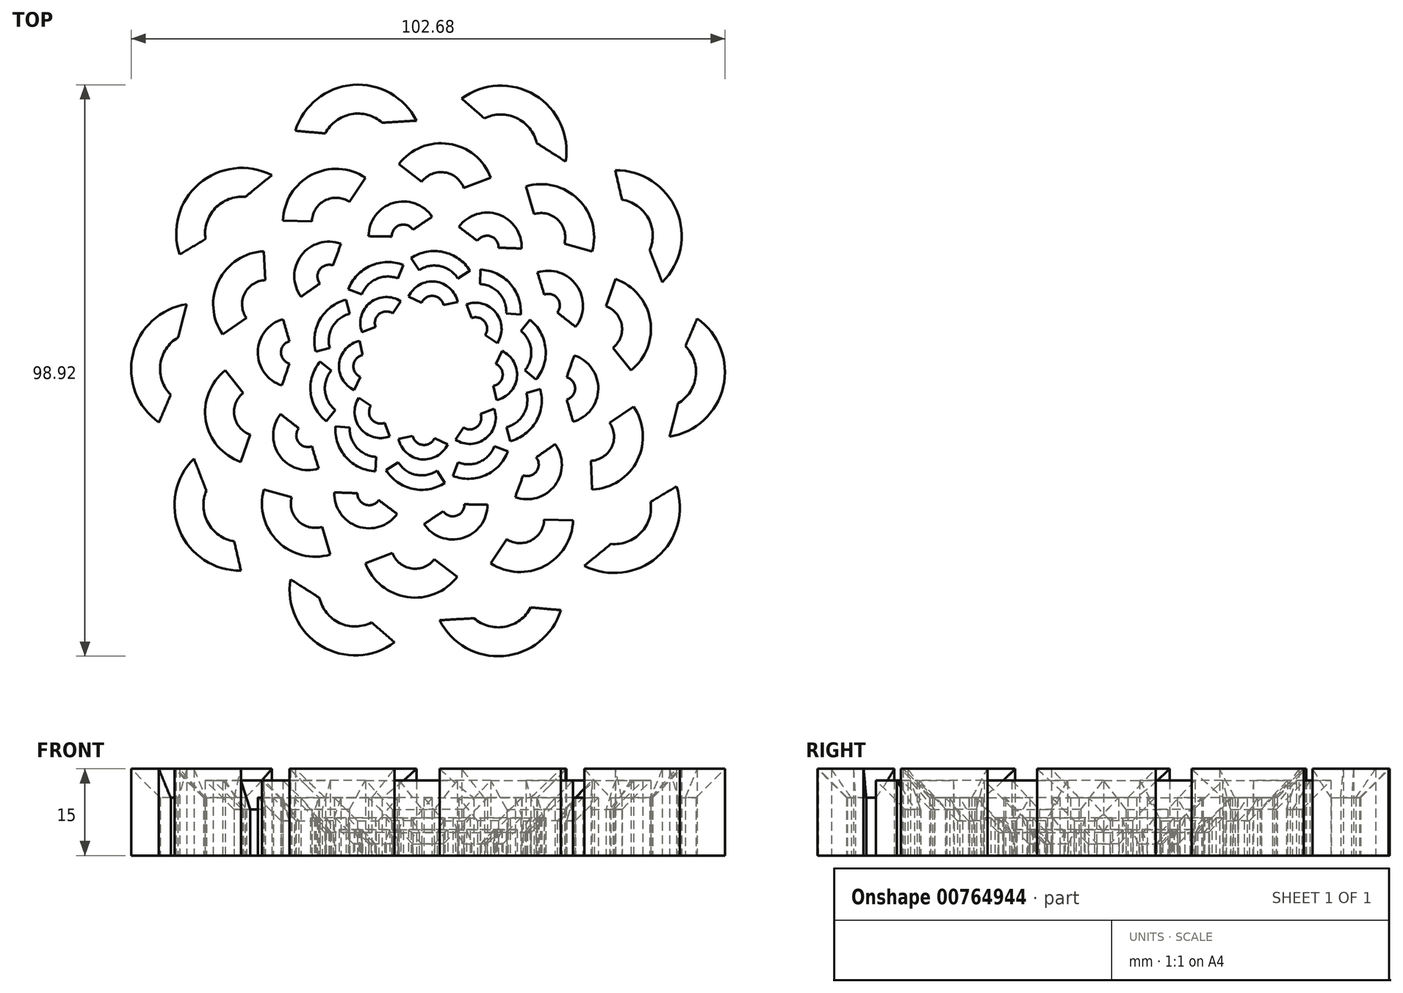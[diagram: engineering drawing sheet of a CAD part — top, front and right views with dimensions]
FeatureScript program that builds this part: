
annotation { "Feature Type Name" : "Feature", "Feature Type Description" : "" }
export const myFeature = defineFeature(function(context is Context, id is Id, definition is map)
    precondition{}
    {
        {
            var Q0;
            Q0=qCreatedBy(makeId("Top.planeOp"),FACE);
            cPlane(context, id + "F0", {"entities" : qUnion([Q0]), "cplaneType" : CPlaneType.OFFSET, "offset" : 30 * mm, "width" : 150 * mm, "height" : 150 * mm});
        }
        {
            var Q0;
            Q0=qCreatedBy(id+"F0.planeOp",FACE);
            var sketch = newSketch(context, id + "F1", { "sketchPlane" : qUnion([Q0])});
            skArc(sketch, "E0", {"start": v(-43.24, 5.7) * mm, "mid": v(-46.3, 1.06) * mm, "end": v(-44.5, -4.21) * mm});
            skArc(sketch, "E1.0", {"start": v(-41.74, 11.46) * mm, "mid": v(-51.04, 2.85) * mm, "end": v(-46.55, -9) * mm});
            skLineSegment(sketch, "E2", {"start": v(-41.74, 11.46) * mm, "end": v(-43.24, 5.7) * mm});
            skLineSegment(sketch, "E3", {"start": v(-44.5, -4.21) * mm, "end": v(-46.55, -9) * mm});
            skArc(sketch, "E4.1.0", {"start": v(-38.34, -20.8) * mm, "mid": v(-38.07, -26.36) * mm, "end": v(-33.53, -29.57) * mm});
            skLineSegment(sketch, "E4.1.1", {"start": v(-40.5, -15.26) * mm, "end": v(-38.34, -20.8) * mm});
            skLineSegment(sketch, "E4.1.2", {"start": v(-33.53, -29.57) * mm, "end": v(-32.36, -34.65) * mm});
            skArc(sketch, "E4.1.3", {"start": v(-40.5, -15.26) * mm, "mid": v(-42.97, -27.7) * mm, "end": v(-32.36, -34.65) * mm});
            skArc(sketch, "E4.2.0", {"start": v(-18.79, -39.36) * mm, "mid": v(-15.3, -43.7) * mm, "end": v(-9.75, -43.63) * mm});
            skLineSegment(sketch, "E4.2.1", {"start": v(-23.8, -36.15) * mm, "end": v(-18.79, -39.36) * mm});
            skLineSegment(sketch, "E4.2.2", {"start": v(-9.75, -43.63) * mm, "end": v(-5.82, -47.05) * mm});
            skArc(sketch, "E4.2.3", {"start": v(-23.8, -36.15) * mm, "mid": v(-18.48, -47.66) * mm, "end": v(-5.82, -47.05) * mm});
            skArc(sketch, "E4.3.0", {"start": v(7.93, -42.89) * mm, "mid": v(13.3, -44.35) * mm, "end": v(17.76, -41.02) * mm});
            skLineSegment(sketch, "E4.3.1", {"start": v(2, -43.24) * mm, "end": v(7.93, -42.89) * mm});
            skLineSegment(sketch, "E4.3.2", {"start": v(17.76, -41.02) * mm, "end": v(22.95, -41.49) * mm});
            skArc(sketch, "E4.3.3", {"start": v(2, -43.24) * mm, "mid": v(13.06, -49.42) * mm, "end": v(22.95, -41.49) * mm});
            skArc(sketch, "E4.4.0", {"start": v(31.63, -30.03) * mm, "mid": v(36.83, -28.06) * mm, "end": v(38.48, -22.75) * mm});
            skLineSegment(sketch, "E4.4.1", {"start": v(27.03, -33.8) * mm, "end": v(31.63, -30.03) * mm});
            skLineSegment(sketch, "E4.4.2", {"start": v(38.48, -22.75) * mm, "end": v(42.95, -20.07) * mm});
            skArc(sketch, "E4.4.3", {"start": v(27.03, -33.8) * mm, "mid": v(39.62, -32.3) * mm, "end": v(42.95, -20.07) * mm});
            skArc(sketch, "E4.5.0", {"start": v(43.24, -5.7) * mm, "mid": v(46.3, -1.06) * mm, "end": v(44.5, 4.21) * mm});
            skLineSegment(sketch, "E4.5.1", {"start": v(41.74, -11.46) * mm, "end": v(43.24, -5.7) * mm});
            skLineSegment(sketch, "E4.5.2", {"start": v(44.5, 4.21) * mm, "end": v(46.55, 9) * mm});
            skArc(sketch, "E4.5.3", {"start": v(41.74, -11.46) * mm, "mid": v(51.04, -2.85) * mm, "end": v(46.55, 9) * mm});
            skArc(sketch, "E4.6.0", {"start": v(38.34, 20.8) * mm, "mid": v(38.07, 26.36) * mm, "end": v(33.53, 29.57) * mm});
            skLineSegment(sketch, "E4.6.1", {"start": v(40.5, 15.26) * mm, "end": v(38.34, 20.8) * mm});
            skLineSegment(sketch, "E4.6.2", {"start": v(33.53, 29.57) * mm, "end": v(32.36, 34.65) * mm});
            skArc(sketch, "E4.6.3", {"start": v(40.5, 15.26) * mm, "mid": v(42.97, 27.7) * mm, "end": v(32.36, 34.65) * mm});
            skArc(sketch, "E4.7.0", {"start": v(18.79, 39.36) * mm, "mid": v(15.3, 43.7) * mm, "end": v(9.75, 43.63) * mm});
            skLineSegment(sketch, "E4.7.1", {"start": v(23.8, 36.15) * mm, "end": v(18.79, 39.36) * mm});
            skLineSegment(sketch, "E4.7.2", {"start": v(9.75, 43.63) * mm, "end": v(5.82, 47.05) * mm});
            skArc(sketch, "E4.7.3", {"start": v(23.8, 36.15) * mm, "mid": v(18.48, 47.66) * mm, "end": v(5.82, 47.05) * mm});
            skArc(sketch, "E4.8.0", {"start": v(-7.93, 42.89) * mm, "mid": v(-13.3, 44.35) * mm, "end": v(-17.76, 41.02) * mm});
            skLineSegment(sketch, "E4.8.1", {"start": v(-2, 43.24) * mm, "end": v(-7.93, 42.89) * mm});
            skLineSegment(sketch, "E4.8.2", {"start": v(-17.76, 41.02) * mm, "end": v(-22.95, 41.49) * mm});
            skArc(sketch, "E4.8.3", {"start": v(-2, 43.24) * mm, "mid": v(-13.06, 49.42) * mm, "end": v(-22.95, 41.49) * mm});
            skArc(sketch, "E4.9.0", {"start": v(-31.63, 30.03) * mm, "mid": v(-36.83, 28.06) * mm, "end": v(-38.48, 22.75) * mm});
            skLineSegment(sketch, "E4.9.1", {"start": v(-27.03, 33.8) * mm, "end": v(-31.63, 30.03) * mm});
            skLineSegment(sketch, "E4.9.2", {"start": v(-38.48, 22.75) * mm, "end": v(-42.95, 20.07) * mm});
            skArc(sketch, "E4.9.3", {"start": v(-27.03, 33.8) * mm, "mid": v(-39.62, 32.3) * mm, "end": v(-42.95, 20.07) * mm});
            skPoint(sketch, "E4.center", {"position": v(0, 0) * mm});
            skArc(sketch, "E5", {"start": v(-35.09, 0) * mm, "mid": v(-38.42, -8.7) * mm, "end": v(-32.4, -15.84) * mm});
            skArc(sketch, "E6.0", {"start": v(-31.97, -3.91) * mm, "mid": v(-33.49, -7.87) * mm, "end": v(-30.75, -11.12) * mm});
            skLineSegment(sketch, "E7", {"start": v(-35.09, 0) * mm, "end": v(-31.97, -3.91) * mm});
            skLineSegment(sketch, "E8", {"start": v(-30.75, -11.12) * mm, "end": v(-32.4, -15.84) * mm});
            skArc(sketch, "E9.1.0", {"start": v(-28.39, -20.62) * mm, "mid": v(-25.96, -29.63) * mm, "end": v(-16.9, -31.86) * mm});
            skArc(sketch, "E9.1.1", {"start": v(-23.57, -21.96) * mm, "mid": v(-22.46, -26.05) * mm, "end": v(-18.34, -27.07) * mm});
            skLineSegment(sketch, "E9.1.2", {"start": v(-28.39, -20.62) * mm, "end": v(-23.57, -21.96) * mm});
            skLineSegment(sketch, "E9.1.3", {"start": v(-18.34, -27.07) * mm, "end": v(-16.9, -31.86) * mm});
            skArc(sketch, "E9.2.0", {"start": v(-10.84, -33.37) * mm, "mid": v(-3.59, -39.23) * mm, "end": v(5.05, -35.71) * mm});
            skArc(sketch, "E9.2.1", {"start": v(-6.16, -31.62) * mm, "mid": v(-2.86, -34.28) * mm, "end": v(1.07, -32.68) * mm});
            skLineSegment(sketch, "E9.2.2", {"start": v(-10.84, -33.37) * mm, "end": v(-6.16, -31.62) * mm});
            skLineSegment(sketch, "E9.2.3", {"start": v(1.07, -32.68) * mm, "end": v(5.05, -35.71) * mm});
            skArc(sketch, "E9.3.0", {"start": v(10.84, -33.37) * mm, "mid": v(20.16, -33.85) * mm, "end": v(25.07, -25.92) * mm});
            skArc(sketch, "E9.3.1", {"start": v(13.6, -29.2) * mm, "mid": v(17.84, -29.41) * mm, "end": v(20.08, -25.81) * mm});
            skLineSegment(sketch, "E9.3.2", {"start": v(10.84, -33.37) * mm, "end": v(13.6, -29.2) * mm});
            skLineSegment(sketch, "E9.3.3", {"start": v(20.08, -25.81) * mm, "end": v(25.07, -25.92) * mm});
            skArc(sketch, "E9.4.0", {"start": v(28.39, -20.62) * mm, "mid": v(36.2, -15.53) * mm, "end": v(35.52, -6.23) * mm});
            skArc(sketch, "E9.4.1", {"start": v(28.16, -15.63) * mm, "mid": v(31.72, -13.31) * mm, "end": v(31.41, -9.08) * mm});
            skLineSegment(sketch, "E9.4.2", {"start": v(28.39, -20.62) * mm, "end": v(28.16, -15.63) * mm});
            skLineSegment(sketch, "E9.4.3", {"start": v(31.41, -9.08) * mm, "end": v(35.52, -6.23) * mm});
            skArc(sketch, "E9.5.0", {"start": v(35.09, 0) * mm, "mid": v(38.42, 8.7) * mm, "end": v(32.4, 15.84) * mm});
            skArc(sketch, "E9.5.1", {"start": v(31.97, 3.91) * mm, "mid": v(33.49, 7.87) * mm, "end": v(30.75, 11.12) * mm});
            skLineSegment(sketch, "E9.5.2", {"start": v(35.09, 0) * mm, "end": v(31.97, 3.91) * mm});
            skLineSegment(sketch, "E9.5.3", {"start": v(30.75, 11.12) * mm, "end": v(32.4, 15.84) * mm});
            skArc(sketch, "E9.6.0", {"start": v(28.39, 20.62) * mm, "mid": v(25.96, 29.63) * mm, "end": v(16.9, 31.86) * mm});
            skArc(sketch, "E9.6.1", {"start": v(23.57, 21.96) * mm, "mid": v(22.46, 26.05) * mm, "end": v(18.34, 27.07) * mm});
            skLineSegment(sketch, "E9.6.2", {"start": v(28.39, 20.62) * mm, "end": v(23.57, 21.96) * mm});
            skLineSegment(sketch, "E9.6.3", {"start": v(18.34, 27.07) * mm, "end": v(16.9, 31.86) * mm});
            skArc(sketch, "E9.7.0", {"start": v(10.84, 33.37) * mm, "mid": v(3.59, 39.23) * mm, "end": v(-5.05, 35.71) * mm});
            skArc(sketch, "E9.7.1", {"start": v(6.16, 31.62) * mm, "mid": v(2.86, 34.28) * mm, "end": v(-1.07, 32.68) * mm});
            skLineSegment(sketch, "E9.7.2", {"start": v(10.84, 33.37) * mm, "end": v(6.16, 31.62) * mm});
            skLineSegment(sketch, "E9.7.3", {"start": v(-1.07, 32.68) * mm, "end": v(-5.05, 35.71) * mm});
            skArc(sketch, "E9.8.0", {"start": v(-10.84, 33.37) * mm, "mid": v(-20.16, 33.85) * mm, "end": v(-25.07, 25.92) * mm});
            skArc(sketch, "E9.8.1", {"start": v(-13.6, 29.2) * mm, "mid": v(-17.84, 29.41) * mm, "end": v(-20.08, 25.81) * mm});
            skLineSegment(sketch, "E9.8.2", {"start": v(-10.84, 33.37) * mm, "end": v(-13.6, 29.2) * mm});
            skLineSegment(sketch, "E9.8.3", {"start": v(-20.08, 25.81) * mm, "end": v(-25.07, 25.92) * mm});
            skArc(sketch, "E9.9.0", {"start": v(-28.39, 20.62) * mm, "mid": v(-36.2, 15.53) * mm, "end": v(-35.52, 6.23) * mm});
            skArc(sketch, "E9.9.1", {"start": v(-28.16, 15.63) * mm, "mid": v(-31.72, 13.31) * mm, "end": v(-31.41, 9.08) * mm});
            skLineSegment(sketch, "E9.9.2", {"start": v(-28.39, 20.62) * mm, "end": v(-28.16, 15.63) * mm});
            skLineSegment(sketch, "E9.9.3", {"start": v(-31.41, 9.08) * mm, "end": v(-35.52, 6.23) * mm});
            skArc(sketch, "E10", {"start": v(-25.51, -7.56) * mm, "mid": v(-25.7, -14.7) * mm, "end": v(-18.93, -16.96) * mm});
            skArc(sketch, "E11.0", {"start": v(-22.36, -10.02) * mm, "mid": v(-22.4, -12.43) * mm, "end": v(-20.1, -13.13) * mm});
            skLineSegment(sketch, "E12", {"start": v(-22.36, -10.02) * mm, "end": v(-25.51, -7.56) * mm});
            skLineSegment(sketch, "E13", {"start": v(-20.1, -13.13) * mm, "end": v(-18.93, -16.96) * mm});
            skArc(sketch, "E14.1.0", {"start": v(-16.2, -21.1) * mm, "mid": v(-12.16, -27) * mm, "end": v(-5.34, -24.84) * mm});
            skLineSegment(sketch, "E14.1.1", {"start": v(-12.2, -21.25) * mm, "end": v(-16.2, -21.1) * mm});
            skArc(sketch, "E14.1.2", {"start": v(-12.2, -21.25) * mm, "mid": v(-10.82, -23.23) * mm, "end": v(-8.54, -22.43) * mm});
            skLineSegment(sketch, "E14.1.3", {"start": v(-8.54, -22.43) * mm, "end": v(-5.34, -24.84) * mm});
            skArc(sketch, "E14.2.0", {"start": v(-0.7, -26.6) * mm, "mid": v(6.03, -28.99) * mm, "end": v(10.28, -23.24) * mm});
            skLineSegment(sketch, "E14.2.1", {"start": v(2.62, -24.36) * mm, "end": v(-0.7, -26.6) * mm});
            skArc(sketch, "E14.2.2", {"start": v(2.62, -24.36) * mm, "mid": v(4.9, -25.15) * mm, "end": v(6.28, -23.17) * mm});
            skLineSegment(sketch, "E14.2.3", {"start": v(6.28, -23.17) * mm, "end": v(10.28, -23.24) * mm});
            skArc(sketch, "E14.3.0", {"start": v(15.07, -21.93) * mm, "mid": v(21.92, -19.9) * mm, "end": v(21.98, -12.76) * mm});
            skLineSegment(sketch, "E14.3.1", {"start": v(16.44, -18.17) * mm, "end": v(15.07, -21.93) * mm});
            skArc(sketch, "E14.3.2", {"start": v(16.44, -18.17) * mm, "mid": v(18.75, -17.47) * mm, "end": v(18.7, -15.05) * mm});
            skLineSegment(sketch, "E14.3.3", {"start": v(18.7, -15.05) * mm, "end": v(21.98, -12.76) * mm});
            skArc(sketch, "E14.4.0", {"start": v(25.08, -8.88) * mm, "mid": v(29.43, -3.22) * mm, "end": v(25.28, 2.6) * mm});
            skLineSegment(sketch, "E14.4.1", {"start": v(23.98, -5.04) * mm, "end": v(25.08, -8.88) * mm});
            skArc(sketch, "E14.4.2", {"start": v(23.98, -5.04) * mm, "mid": v(25.43, -3.11) * mm, "end": v(23.97, -1.19) * mm});
            skLineSegment(sketch, "E14.4.3", {"start": v(23.97, -1.19) * mm, "end": v(25.28, 2.6) * mm});
            skArc(sketch, "E14.5.0", {"start": v(25.51, 7.56) * mm, "mid": v(25.7, 14.7) * mm, "end": v(18.93, 16.96) * mm});
            skLineSegment(sketch, "E14.5.1", {"start": v(22.36, 10.02) * mm, "end": v(25.51, 7.56) * mm});
            skArc(sketch, "E14.5.2", {"start": v(22.36, 10.02) * mm, "mid": v(22.4, 12.43) * mm, "end": v(20.1, 13.13) * mm});
            skLineSegment(sketch, "E14.5.3", {"start": v(20.1, 13.13) * mm, "end": v(18.93, 16.96) * mm});
            skArc(sketch, "E14.6.0", {"start": v(16.2, 21.1) * mm, "mid": v(12.16, 27) * mm, "end": v(5.34, 24.84) * mm});
            skLineSegment(sketch, "E14.6.1", {"start": v(12.2, 21.25) * mm, "end": v(16.2, 21.1) * mm});
            skArc(sketch, "E14.6.2", {"start": v(12.2, 21.25) * mm, "mid": v(10.82, 23.23) * mm, "end": v(8.54, 22.43) * mm});
            skLineSegment(sketch, "E14.6.3", {"start": v(8.54, 22.43) * mm, "end": v(5.34, 24.84) * mm});
            skArc(sketch, "E14.7.0", {"start": v(0.7, 26.6) * mm, "mid": v(-6.03, 28.99) * mm, "end": v(-10.28, 23.24) * mm});
            skLineSegment(sketch, "E14.7.1", {"start": v(-2.62, 24.36) * mm, "end": v(0.7, 26.6) * mm});
            skArc(sketch, "E14.7.2", {"start": v(-2.62, 24.36) * mm, "mid": v(-4.9, 25.15) * mm, "end": v(-6.28, 23.17) * mm});
            skLineSegment(sketch, "E14.7.3", {"start": v(-6.28, 23.17) * mm, "end": v(-10.28, 23.24) * mm});
            skArc(sketch, "E14.8.0", {"start": v(-15.07, 21.93) * mm, "mid": v(-21.92, 19.9) * mm, "end": v(-21.98, 12.76) * mm});
            skLineSegment(sketch, "E14.8.1", {"start": v(-16.44, 18.17) * mm, "end": v(-15.07, 21.93) * mm});
            skArc(sketch, "E14.8.2", {"start": v(-16.44, 18.17) * mm, "mid": v(-18.75, 17.47) * mm, "end": v(-18.7, 15.05) * mm});
            skLineSegment(sketch, "E14.8.3", {"start": v(-18.7, 15.05) * mm, "end": v(-21.98, 12.76) * mm});
            skArc(sketch, "E14.9.0", {"start": v(-25.08, 8.88) * mm, "mid": v(-29.43, 3.22) * mm, "end": v(-25.28, -2.6) * mm});
            skLineSegment(sketch, "E14.9.1", {"start": v(-23.98, 5.04) * mm, "end": v(-25.08, 8.88) * mm});
            skArc(sketch, "E14.9.2", {"start": v(-23.98, 5.04) * mm, "mid": v(-25.43, 3.11) * mm, "end": v(-23.97, 1.19) * mm});
            skLineSegment(sketch, "E14.9.3", {"start": v(-23.97, 1.19) * mm, "end": v(-25.28, -2.6) * mm});
            skArc(sketch, "E15", {"start": v(-14.18, 12.24) * mm, "mid": v(-18.68, 8.84) * mm, "end": v(-19.4, 3.24) * mm});
            skArc(sketch, "E16.0", {"start": v(-13.56, 9.82) * mm, "mid": v(-16.52, 7.58) * mm, "end": v(-17, 3.9) * mm});
            skLineSegment(sketch, "E17", {"start": v(-14.18, 12.24) * mm, "end": v(-13.56, 9.82) * mm});
            skLineSegment(sketch, "E18", {"start": v(-17, 3.9) * mm, "end": v(-19.4, 3.24) * mm});
            skArc(sketch, "E19.1.0", {"start": v(-16.74, -0.03) * mm, "mid": v(-17.82, -3.58) * mm, "end": v(-16.05, -6.83) * mm});
            skArc(sketch, "E19.1.1", {"start": v(-18.67, 1.57) * mm, "mid": v(-20.3, -3.83) * mm, "end": v(-17.6, -8.79) * mm});
            skLineSegment(sketch, "E19.1.2", {"start": v(-18.67, 1.57) * mm, "end": v(-16.74, -0.03) * mm});
            skLineSegment(sketch, "E19.1.3", {"start": v(-16.05, -6.83) * mm, "end": v(-17.6, -8.79) * mm});
            skArc(sketch, "E19.2.0", {"start": v(-13.53, -9.86) * mm, "mid": v(-12.32, -13.37) * mm, "end": v(-8.97, -14.96) * mm});
            skArc(sketch, "E19.2.1", {"start": v(-16.02, -9.7) * mm, "mid": v(-14.18, -15.04) * mm, "end": v(-9.08, -17.46) * mm});
            skLineSegment(sketch, "E19.2.2", {"start": v(-16.02, -9.7) * mm, "end": v(-13.53, -9.86) * mm});
            skLineSegment(sketch, "E19.2.3", {"start": v(-8.97, -14.96) * mm, "end": v(-9.08, -17.46) * mm});
            skArc(sketch, "E19.3.0", {"start": v(-5.15, -15.93) * mm, "mid": v(-2.1, -18.05) * mm, "end": v(1.54, -17.37) * mm});
            skArc(sketch, "E19.3.1", {"start": v(-7.26, -17.27) * mm, "mid": v(-2.63, -20.5) * mm, "end": v(2.91, -19.46) * mm});
            skLineSegment(sketch, "E19.3.2", {"start": v(-7.26, -17.27) * mm, "end": v(-5.15, -15.93) * mm});
            skLineSegment(sketch, "E19.3.3", {"start": v(1.54, -17.37) * mm, "end": v(2.91, -19.46) * mm});
            skArc(sketch, "E19.4.0", {"start": v(5.2, -15.91) * mm, "mid": v(8.9, -15.84) * mm, "end": v(11.46, -13.15) * mm});
            skArc(sketch, "E19.4.1", {"start": v(4.28, -18.24) * mm, "mid": v(9.92, -18.13) * mm, "end": v(13.8, -14.03) * mm});
            skLineSegment(sketch, "E19.4.2", {"start": v(4.28, -18.24) * mm, "end": v(5.2, -15.91) * mm});
            skLineSegment(sketch, "E19.4.3", {"start": v(11.46, -13.15) * mm, "end": v(13.8, -14.03) * mm});
            skArc(sketch, "E19.5.0", {"start": v(13.56, -9.82) * mm, "mid": v(16.52, -7.58) * mm, "end": v(17, -3.9) * mm});
            skArc(sketch, "E19.5.1", {"start": v(14.18, -12.24) * mm, "mid": v(18.68, -8.84) * mm, "end": v(19.4, -3.24) * mm});
            skLineSegment(sketch, "E19.5.2", {"start": v(14.18, -12.24) * mm, "end": v(13.56, -9.82) * mm});
            skLineSegment(sketch, "E19.5.3", {"start": v(17, -3.9) * mm, "end": v(19.4, -3.24) * mm});
            skArc(sketch, "E19.6.0", {"start": v(16.74, 0.03) * mm, "mid": v(17.82, 3.58) * mm, "end": v(16.05, 6.83) * mm});
            skArc(sketch, "E19.6.1", {"start": v(18.67, -1.57) * mm, "mid": v(20.3, 3.83) * mm, "end": v(17.6, 8.79) * mm});
            skLineSegment(sketch, "E19.6.2", {"start": v(18.67, -1.57) * mm, "end": v(16.74, 0.03) * mm});
            skLineSegment(sketch, "E19.6.3", {"start": v(16.05, 6.83) * mm, "end": v(17.6, 8.79) * mm});
            skArc(sketch, "E19.7.0", {"start": v(13.53, 9.86) * mm, "mid": v(12.32, 13.37) * mm, "end": v(8.97, 14.96) * mm});
            skArc(sketch, "E19.7.1", {"start": v(16.02, 9.7) * mm, "mid": v(14.18, 15.04) * mm, "end": v(9.08, 17.46) * mm});
            skLineSegment(sketch, "E19.7.2", {"start": v(16.02, 9.7) * mm, "end": v(13.53, 9.86) * mm});
            skLineSegment(sketch, "E19.7.3", {"start": v(8.97, 14.96) * mm, "end": v(9.08, 17.46) * mm});
            skArc(sketch, "E19.8.0", {"start": v(5.15, 15.93) * mm, "mid": v(2.1, 18.05) * mm, "end": v(-1.54, 17.37) * mm});
            skArc(sketch, "E19.8.1", {"start": v(7.26, 17.27) * mm, "mid": v(2.63, 20.5) * mm, "end": v(-2.91, 19.46) * mm});
            skLineSegment(sketch, "E19.8.2", {"start": v(7.26, 17.27) * mm, "end": v(5.15, 15.93) * mm});
            skLineSegment(sketch, "E19.8.3", {"start": v(-1.54, 17.37) * mm, "end": v(-2.91, 19.46) * mm});
            skArc(sketch, "E19.9.0", {"start": v(-5.2, 15.91) * mm, "mid": v(-8.9, 15.84) * mm, "end": v(-11.46, 13.15) * mm});
            skArc(sketch, "E19.9.1", {"start": v(-4.28, 18.24) * mm, "mid": v(-9.92, 18.13) * mm, "end": v(-13.8, 14.03) * mm});
            skLineSegment(sketch, "E19.9.2", {"start": v(-4.28, 18.24) * mm, "end": v(-5.2, 15.91) * mm});
            skLineSegment(sketch, "E19.9.3", {"start": v(-11.46, 13.15) * mm, "end": v(-13.8, 14.03) * mm});
            skArc(sketch, "E20", {"start": v(-11.82, 5.12) * mm, "mid": v(-15.37, 1.22) * mm, "end": v(-12.78, -3.38) * mm});
            skArc(sketch, "E21.0", {"start": v(-11.31, 2.67) * mm, "mid": v(-12.9, 0.94) * mm, "end": v(-11.74, -1.1) * mm});
            skLineSegment(sketch, "E22", {"start": v(-11.82, 5.12) * mm, "end": v(-11.31, 2.67) * mm});
            skLineSegment(sketch, "E23", {"start": v(-11.74, -1.1) * mm, "end": v(-12.78, -3.38) * mm});
            skArc(sketch, "E24.1.0", {"start": v(-11.98, -4.74) * mm, "mid": v(-11.73, -10.01) * mm, "end": v(-6.65, -11.43) * mm});
            skArc(sketch, "E24.2.0", {"start": v(-5.12, -11.82) * mm, "mid": v(-1.22, -15.37) * mm, "end": v(3.38, -12.78) * mm});
            skArc(sketch, "E25.3.3.0", {"start": v(4.74, -11.98) * mm, "mid": v(10.01, -11.73) * mm, "end": v(11.43, -6.65) * mm});
            skArc(sketch, "E25.3.4.0", {"start": v(11.82, -5.12) * mm, "mid": v(15.37, -1.22) * mm, "end": v(12.78, 3.38) * mm});
            skArc(sketch, "E25.3.5.0", {"start": v(11.98, 4.74) * mm, "mid": v(11.73, 10.01) * mm, "end": v(6.65, 11.43) * mm});
            skArc(sketch, "E25.3.6.0", {"start": v(5.12, 11.82) * mm, "mid": v(1.22, 15.37) * mm, "end": v(-3.38, 12.78) * mm});
            skArc(sketch, "E25.3.7.0", {"start": v(-4.74, 11.98) * mm, "mid": v(-10.01, 11.73) * mm, "end": v(-11.43, 6.65) * mm});
            skLineSegment(sketch, "E26.1.0", {"start": v(-7.52, -9.08) * mm, "end": v(-6.65, -11.43) * mm});
            skArc(sketch, "E26.1.1", {"start": v(-9.89, -6.11) * mm, "mid": v(-9.78, -8.45) * mm, "end": v(-7.52, -9.08) * mm});
            skLineSegment(sketch, "E26.1.2", {"start": v(-11.98, -4.74) * mm, "end": v(-9.89, -6.11) * mm});
            skLineSegment(sketch, "E26.2.0", {"start": v(1.1, -11.74) * mm, "end": v(3.38, -12.78) * mm});
            skArc(sketch, "E26.2.1", {"start": v(-2.67, -11.31) * mm, "mid": v(-0.94, -12.9) * mm, "end": v(1.1, -11.74) * mm});
            skLineSegment(sketch, "E26.2.2", {"start": v(-5.12, -11.82) * mm, "end": v(-2.67, -11.31) * mm});
            skLineSegment(sketch, "E26.3.0", {"start": v(9.08, -7.52) * mm, "end": v(11.43, -6.65) * mm});
            skArc(sketch, "E26.3.1", {"start": v(6.11, -9.89) * mm, "mid": v(8.45, -9.78) * mm, "end": v(9.08, -7.52) * mm});
            skLineSegment(sketch, "E26.3.2", {"start": v(4.74, -11.98) * mm, "end": v(6.11, -9.89) * mm});
            skLineSegment(sketch, "E26.4.0", {"start": v(11.74, 1.1) * mm, "end": v(12.78, 3.38) * mm});
            skArc(sketch, "E26.4.1", {"start": v(11.31, -2.67) * mm, "mid": v(12.9, -0.94) * mm, "end": v(11.74, 1.1) * mm});
            skLineSegment(sketch, "E26.4.2", {"start": v(11.82, -5.12) * mm, "end": v(11.31, -2.67) * mm});
            skLineSegment(sketch, "E26.5.0", {"start": v(7.52, 9.08) * mm, "end": v(6.65, 11.43) * mm});
            skArc(sketch, "E26.5.1", {"start": v(9.89, 6.11) * mm, "mid": v(9.78, 8.45) * mm, "end": v(7.52, 9.08) * mm});
            skLineSegment(sketch, "E26.5.2", {"start": v(11.98, 4.74) * mm, "end": v(9.89, 6.11) * mm});
            skLineSegment(sketch, "E26.6.0", {"start": v(-1.1, 11.74) * mm, "end": v(-3.38, 12.78) * mm});
            skArc(sketch, "E26.6.1", {"start": v(2.67, 11.31) * mm, "mid": v(0.94, 12.9) * mm, "end": v(-1.1, 11.74) * mm});
            skLineSegment(sketch, "E26.6.2", {"start": v(5.12, 11.82) * mm, "end": v(2.67, 11.31) * mm});
            skLineSegment(sketch, "E26.7.0", {"start": v(-9.08, 7.52) * mm, "end": v(-11.43, 6.65) * mm});
            skArc(sketch, "E26.7.1", {"start": v(-6.11, 9.89) * mm, "mid": v(-8.45, 9.78) * mm, "end": v(-9.08, 7.52) * mm});
            skLineSegment(sketch, "E26.7.2", {"start": v(-4.74, 11.98) * mm, "end": v(-6.11, 9.89) * mm});
            skSolve(sketch);
        }
        {
            var Q0;
            Q0=makeQuery(id+"F1.imprint","IMPRINT",FACE,{"disambiguationData":[TD([[makeQuery(id+"F1.imprint","IMPRINT",EDGE,{"derivedFrom":sQuery(id+"F1.wireOp",EDGE,"E4.3.0")}),-1.0]])]});
            var Q1;
            Q1=makeQuery(id+"F1.imprint","IMPRINT",FACE,{"disambiguationData":[TD([[makeQuery(id+"F1.imprint","IMPRINT",EDGE,{"derivedFrom":sQuery(id+"F1.wireOp",EDGE,"E4.2.0")}),-1.0]])]});
            var Q2;
            Q2=makeQuery(id+"F1.imprint","IMPRINT",FACE,{"disambiguationData":[TD([[makeQuery(id+"F1.imprint","IMPRINT",EDGE,{"derivedFrom":sQuery(id+"F1.wireOp",EDGE,"E4.1.0")}),-1.0]])]});
            var Q3;
            Q3=makeQuery(id+"F1.imprint","IMPRINT",FACE,{"disambiguationData":[TD([[makeQuery(id+"F1.imprint","IMPRINT",EDGE,{"derivedFrom":sQuery(id+"F1.wireOp",EDGE,"E0")}),-1.0]])]});
            var Q4;
            Q4=makeQuery(id+"F1.imprint","IMPRINT",FACE,{"disambiguationData":[TD([[makeQuery(id+"F1.imprint","IMPRINT",EDGE,{"derivedFrom":sQuery(id+"F1.wireOp",EDGE,"E4.9.0")}),-1.0]])]});
            var Q5;
            Q5=makeQuery(id+"F1.imprint","IMPRINT",FACE,{"disambiguationData":[TD([[makeQuery(id+"F1.imprint","IMPRINT",EDGE,{"derivedFrom":sQuery(id+"F1.wireOp",EDGE,"E4.8.0")}),-1.0]])]});
            var Q6;
            Q6=makeQuery(id+"F1.imprint","IMPRINT",FACE,{"disambiguationData":[TD([[makeQuery(id+"F1.imprint","IMPRINT",EDGE,{"derivedFrom":sQuery(id+"F1.wireOp",EDGE,"E4.7.0")}),-1.0]])]});
            var Q7;
            Q7=makeQuery(id+"F1.imprint","IMPRINT",FACE,{"disambiguationData":[TD([[makeQuery(id+"F1.imprint","IMPRINT",EDGE,{"derivedFrom":sQuery(id+"F1.wireOp",EDGE,"E4.6.0")}),-1.0]])]});
            var Q8;
            Q8=makeQuery(id+"F1.imprint","IMPRINT",FACE,{"disambiguationData":[TD([[makeQuery(id+"F1.imprint","IMPRINT",EDGE,{"derivedFrom":sQuery(id+"F1.wireOp",EDGE,"E4.5.0")}),-1.0]])]});
            var Q9;
            Q9=makeQuery(id+"F1.imprint","IMPRINT",FACE,{"disambiguationData":[TD([[makeQuery(id+"F1.imprint","IMPRINT",EDGE,{"derivedFrom":sQuery(id+"F1.wireOp",EDGE,"E4.4.0")}),-1.0]])]});
            extrude(context, id + "F2", {"entities" : qUnion([Q0, Q1, Q2, Q3, Q4, Q5, Q6, Q7, Q8, Q9]), "depth" : 15 * mm, "offsetDistance" : 25 * mm});
        }
        {
            var Q0;
            Q0=makeQuery(id+"F1.imprint","IMPRINT",FACE,{"disambiguationData":[TD([[makeQuery(id+"F1.imprint","IMPRINT",EDGE,{"derivedFrom":sQuery(id+"F1.wireOp",EDGE,"E9.2.0")}),1.0]])]});
            var Q1;
            Q1=makeQuery(id+"F1.imprint","IMPRINT",FACE,{"disambiguationData":[TD([[makeQuery(id+"F1.imprint","IMPRINT",EDGE,{"derivedFrom":sQuery(id+"F1.wireOp",EDGE,"E9.1.0")}),1.0]])]});
            var Q2;
            Q2=makeQuery(id+"F1.imprint","IMPRINT",FACE,{"disambiguationData":[TD([[makeQuery(id+"F1.imprint","IMPRINT",EDGE,{"derivedFrom":sQuery(id+"F1.wireOp",EDGE,"E5")}),1.0]])]});
            var Q3;
            Q3=makeQuery(id+"F1.imprint","IMPRINT",FACE,{"disambiguationData":[TD([[makeQuery(id+"F1.imprint","IMPRINT",EDGE,{"derivedFrom":sQuery(id+"F1.wireOp",EDGE,"E9.9.0")}),1.0]])]});
            var Q4;
            Q4=makeQuery(id+"F1.imprint","IMPRINT",FACE,{"disambiguationData":[TD([[makeQuery(id+"F1.imprint","IMPRINT",EDGE,{"derivedFrom":sQuery(id+"F1.wireOp",EDGE,"E9.8.0")}),1.0]])]});
            var Q5;
            Q5=makeQuery(id+"F1.imprint","IMPRINT",FACE,{"disambiguationData":[TD([[makeQuery(id+"F1.imprint","IMPRINT",EDGE,{"derivedFrom":sQuery(id+"F1.wireOp",EDGE,"E9.7.0")}),1.0]])]});
            var Q6;
            Q6=makeQuery(id+"F1.imprint","IMPRINT",FACE,{"disambiguationData":[TD([[makeQuery(id+"F1.imprint","IMPRINT",EDGE,{"derivedFrom":sQuery(id+"F1.wireOp",EDGE,"E9.6.0")}),1.0]])]});
            var Q7;
            Q7=makeQuery(id+"F1.imprint","IMPRINT",FACE,{"disambiguationData":[TD([[makeQuery(id+"F1.imprint","IMPRINT",EDGE,{"derivedFrom":sQuery(id+"F1.wireOp",EDGE,"E9.5.0")}),1.0]])]});
            var Q8;
            Q8=makeQuery(id+"F1.imprint","IMPRINT",FACE,{"disambiguationData":[TD([[makeQuery(id+"F1.imprint","IMPRINT",EDGE,{"derivedFrom":sQuery(id+"F1.wireOp",EDGE,"E9.4.0")}),1.0]])]});
            var Q9;
            Q9=makeQuery(id+"F1.imprint","IMPRINT",FACE,{"disambiguationData":[TD([[makeQuery(id+"F1.imprint","IMPRINT",EDGE,{"derivedFrom":sQuery(id+"F1.wireOp",EDGE,"E9.3.0")}),1.0]])]});
            extrude(context, id + "F3", {"entities" : qUnion([Q0, Q1, Q2, Q3, Q4, Q5, Q6, Q7, Q8, Q9]), "depth" : 13 * mm, "offsetDistance" : 25 * mm});
        }
        {
            var Q0;
            Q0=makeQuery(id+"F1.imprint","IMPRINT",FACE,{"disambiguationData":[TD([[makeQuery(id+"F1.imprint","IMPRINT",EDGE,{"derivedFrom":sQuery(id+"F1.wireOp",EDGE,"E14.3.0")}),1.0]])]});
            var Q1;
            Q1=makeQuery(id+"F1.imprint","IMPRINT",FACE,{"disambiguationData":[TD([[makeQuery(id+"F1.imprint","IMPRINT",EDGE,{"derivedFrom":sQuery(id+"F1.wireOp",EDGE,"E14.2.0")}),1.0]])]});
            var Q2;
            Q2=makeQuery(id+"F1.imprint","IMPRINT",FACE,{"disambiguationData":[TD([[makeQuery(id+"F1.imprint","IMPRINT",EDGE,{"derivedFrom":sQuery(id+"F1.wireOp",EDGE,"E14.1.0")}),1.0]])]});
            var Q3;
            Q3=makeQuery(id+"F1.imprint","IMPRINT",FACE,{"disambiguationData":[TD([[makeQuery(id+"F1.imprint","IMPRINT",EDGE,{"derivedFrom":sQuery(id+"F1.wireOp",EDGE,"E10")}),1.0]])]});
            var Q4;
            Q4=makeQuery(id+"F1.imprint","IMPRINT",FACE,{"disambiguationData":[TD([[makeQuery(id+"F1.imprint","IMPRINT",EDGE,{"derivedFrom":sQuery(id+"F1.wireOp",EDGE,"E14.9.0")}),1.0]])]});
            var Q5;
            Q5=makeQuery(id+"F1.imprint","IMPRINT",FACE,{"disambiguationData":[TD([[makeQuery(id+"F1.imprint","IMPRINT",EDGE,{"derivedFrom":sQuery(id+"F1.wireOp",EDGE,"E14.8.0")}),1.0]])]});
            var Q6;
            Q6=makeQuery(id+"F1.imprint","IMPRINT",FACE,{"disambiguationData":[TD([[makeQuery(id+"F1.imprint","IMPRINT",EDGE,{"derivedFrom":sQuery(id+"F1.wireOp",EDGE,"E14.7.0")}),1.0]])]});
            var Q7;
            Q7=makeQuery(id+"F1.imprint","IMPRINT",FACE,{"disambiguationData":[TD([[makeQuery(id+"F1.imprint","IMPRINT",EDGE,{"derivedFrom":sQuery(id+"F1.wireOp",EDGE,"E14.6.0")}),1.0]])]});
            var Q8;
            Q8=makeQuery(id+"F1.imprint","IMPRINT",FACE,{"disambiguationData":[TD([[makeQuery(id+"F1.imprint","IMPRINT",EDGE,{"derivedFrom":sQuery(id+"F1.wireOp",EDGE,"E14.5.0")}),1.0]])]});
            var Q9;
            Q9=makeQuery(id+"F1.imprint","IMPRINT",FACE,{"disambiguationData":[TD([[makeQuery(id+"F1.imprint","IMPRINT",EDGE,{"derivedFrom":sQuery(id+"F1.wireOp",EDGE,"E14.4.0")}),1.0]])]});
            extrude(context, id + "F4", {"entities" : qUnion([Q0, Q1, Q2, Q3, Q4, Q5, Q6, Q7, Q8, Q9]), "depth" : 11 * mm, "offsetDistance" : 25 * mm});
        }
        {
            var Q0;
            Q0=makeQuery(id+"F1.imprint","IMPRINT",FACE,{"disambiguationData":[TD([[makeQuery(id+"F1.imprint","IMPRINT",EDGE,{"derivedFrom":sQuery(id+"F1.wireOp",EDGE,"E19.4.0")}),-1.0]])]});
            var Q1;
            Q1=makeQuery(id+"F1.imprint","IMPRINT",FACE,{"disambiguationData":[TD([[makeQuery(id+"F1.imprint","IMPRINT",EDGE,{"derivedFrom":sQuery(id+"F1.wireOp",EDGE,"E19.3.0")}),-1.0]])]});
            var Q2;
            Q2=makeQuery(id+"F1.imprint","IMPRINT",FACE,{"disambiguationData":[TD([[makeQuery(id+"F1.imprint","IMPRINT",EDGE,{"derivedFrom":sQuery(id+"F1.wireOp",EDGE,"E19.2.0")}),-1.0]])]});
            var Q3;
            Q3=makeQuery(id+"F1.imprint","IMPRINT",FACE,{"disambiguationData":[TD([[makeQuery(id+"F1.imprint","IMPRINT",EDGE,{"derivedFrom":sQuery(id+"F1.wireOp",EDGE,"E19.1.0")}),-1.0]])]});
            var Q4;
            Q4=makeQuery(id+"F1.imprint","IMPRINT",FACE,{"disambiguationData":[TD([[makeQuery(id+"F1.imprint","IMPRINT",EDGE,{"derivedFrom":sQuery(id+"F1.wireOp",EDGE,"E15")}),1.0]])]});
            var Q5;
            Q5=makeQuery(id+"F1.imprint","IMPRINT",FACE,{"disambiguationData":[TD([[makeQuery(id+"F1.imprint","IMPRINT",EDGE,{"derivedFrom":sQuery(id+"F1.wireOp",EDGE,"E19.9.0")}),-1.0]])]});
            var Q6;
            Q6=makeQuery(id+"F1.imprint","IMPRINT",FACE,{"disambiguationData":[TD([[makeQuery(id+"F1.imprint","IMPRINT",EDGE,{"derivedFrom":sQuery(id+"F1.wireOp",EDGE,"E19.8.0")}),-1.0]])]});
            var Q7;
            Q7=makeQuery(id+"F1.imprint","IMPRINT",FACE,{"disambiguationData":[TD([[makeQuery(id+"F1.imprint","IMPRINT",EDGE,{"derivedFrom":sQuery(id+"F1.wireOp",EDGE,"E19.7.0")}),-1.0]])]});
            var Q8;
            Q8=makeQuery(id+"F1.imprint","IMPRINT",FACE,{"disambiguationData":[TD([[makeQuery(id+"F1.imprint","IMPRINT",EDGE,{"derivedFrom":sQuery(id+"F1.wireOp",EDGE,"E19.6.0")}),-1.0]])]});
            var Q9;
            Q9=makeQuery(id+"F1.imprint","IMPRINT",FACE,{"disambiguationData":[TD([[makeQuery(id+"F1.imprint","IMPRINT",EDGE,{"derivedFrom":sQuery(id+"F1.wireOp",EDGE,"E19.5.0")}),-1.0]])]});
            extrude(context, id + "F5", {"entities" : qUnion([Q0, Q1, Q2, Q3, Q4, Q5, Q6, Q7, Q8, Q9]), "depth" : 9 * mm, "offsetDistance" : 25 * mm});
        }
        {
            var Q0;
            Q0=makeQuery(id+"F1.imprint","IMPRINT",FACE,{"disambiguationData":[TD([[makeQuery(id+"F1.imprint","IMPRINT",EDGE,{"derivedFrom":sQuery(id+"F1.wireOp",EDGE,"E25.3.3.0")}),1.0]])]});
            var Q1;
            Q1=makeQuery(id+"F1.imprint","IMPRINT",FACE,{"disambiguationData":[TD([[makeQuery(id+"F1.imprint","IMPRINT",EDGE,{"derivedFrom":sQuery(id+"F1.wireOp",EDGE,"E24.2.0")}),1.0]])]});
            var Q2;
            Q2=makeQuery(id+"F1.imprint","IMPRINT",FACE,{"disambiguationData":[TD([[makeQuery(id+"F1.imprint","IMPRINT",EDGE,{"derivedFrom":sQuery(id+"F1.wireOp",EDGE,"E24.1.0")}),1.0]])]});
            var Q3;
            Q3=makeQuery(id+"F1.imprint","IMPRINT",FACE,{"disambiguationData":[TD([[makeQuery(id+"F1.imprint","IMPRINT",EDGE,{"derivedFrom":sQuery(id+"F1.wireOp",EDGE,"E20")}),1.0]])]});
            var Q4;
            Q4=makeQuery(id+"F1.imprint","IMPRINT",FACE,{"disambiguationData":[TD([[makeQuery(id+"F1.imprint","IMPRINT",EDGE,{"derivedFrom":sQuery(id+"F1.wireOp",EDGE,"E25.3.7.0")}),1.0]])]});
            var Q5;
            Q5=makeQuery(id+"F1.imprint","IMPRINT",FACE,{"disambiguationData":[TD([[makeQuery(id+"F1.imprint","IMPRINT",EDGE,{"derivedFrom":sQuery(id+"F1.wireOp",EDGE,"E25.3.6.0")}),1.0]])]});
            var Q6;
            Q6=makeQuery(id+"F1.imprint","IMPRINT",FACE,{"disambiguationData":[TD([[makeQuery(id+"F1.imprint","IMPRINT",EDGE,{"derivedFrom":sQuery(id+"F1.wireOp",EDGE,"E25.3.5.0")}),1.0]])]});
            var Q7;
            Q7=makeQuery(id+"F1.imprint","IMPRINT",FACE,{"disambiguationData":[TD([[makeQuery(id+"F1.imprint","IMPRINT",EDGE,{"derivedFrom":sQuery(id+"F1.wireOp",EDGE,"E25.3.4.0")}),1.0]])]});
            extrude(context, id + "F6", {"entities" : qUnion([Q0, Q1, Q2, Q3, Q4, Q5, Q6, Q7]), "depth" : 7 * mm, "offsetDistance" : 25 * mm});
        }
        {
            var Q0;
            Q0=makeQuery(id+"F2.opExtrude","CAP_EDGE",EDGE,{"disambiguationData":[OSD([sQuery(id+"F1.wireOp",EDGE,"E0")])],"isStart":false});
            var Q1;
            Q1=makeQuery(id+"F3.opExtrude","CAP_EDGE",EDGE,{"disambiguationData":[OSD([sQuery(id+"F1.wireOp",EDGE,"E6.0")])],"isStart":false});
            var Q2;
            Q2=makeQuery(id+"F2.opExtrude","CAP_EDGE",EDGE,{"disambiguationData":[OSD([sQuery(id+"F1.wireOp",EDGE,"E4.1.0")])],"isStart":false});
            var Q3;
            Q3=makeQuery(id+"F3.opExtrude","CAP_EDGE",EDGE,{"disambiguationData":[OSD([sQuery(id+"F1.wireOp",EDGE,"E9.1.1")])],"isStart":false});
            var Q4;
            Q4=makeQuery(id+"F2.opExtrude","CAP_EDGE",EDGE,{"disambiguationData":[OSD([sQuery(id+"F1.wireOp",EDGE,"E4.2.0")])],"isStart":false});
            var Q5;
            Q5=makeQuery(id+"F2.opExtrude","CAP_EDGE",EDGE,{"disambiguationData":[OSD([sQuery(id+"F1.wireOp",EDGE,"E4.3.0")])],"isStart":false});
            var Q6;
            Q6=makeQuery(id+"F3.opExtrude","CAP_EDGE",EDGE,{"disambiguationData":[OSD([sQuery(id+"F1.wireOp",EDGE,"E9.2.1")])],"isStart":false});
            var Q7;
            Q7=makeQuery(id+"F4.opExtrude","CAP_EDGE",EDGE,{"disambiguationData":[OSD([sQuery(id+"F1.wireOp",EDGE,"E14.1.2")])],"isStart":false});
            var Q8;
            Q8=makeQuery(id+"F4.opExtrude","CAP_EDGE",EDGE,{"disambiguationData":[OSD([sQuery(id+"F1.wireOp",EDGE,"E11.0")])],"isStart":false});
            var Q9;
            Q9=makeQuery(id+"F4.opExtrude","CAP_EDGE",EDGE,{"disambiguationData":[OSD([sQuery(id+"F1.wireOp",EDGE,"E14.9.2")])],"isStart":false});
            var Q10;
            Q10=makeQuery(id+"F4.opExtrude","CAP_EDGE",EDGE,{"disambiguationData":[OSD([sQuery(id+"F1.wireOp",EDGE,"E14.8.2")])],"isStart":false});
            var Q11;
            Q11=makeQuery(id+"F3.opExtrude","CAP_EDGE",EDGE,{"disambiguationData":[OSD([sQuery(id+"F1.wireOp",EDGE,"E9.9.1")])],"isStart":false});
            var Q12;
            Q12=makeQuery(id+"F3.opExtrude","CAP_EDGE",EDGE,{"disambiguationData":[OSD([sQuery(id+"F1.wireOp",EDGE,"E9.8.1")])],"isStart":false});
            var Q13;
            Q13=makeQuery(id+"F2.opExtrude","CAP_EDGE",EDGE,{"disambiguationData":[OSD([sQuery(id+"F1.wireOp",EDGE,"E4.9.0")])],"isStart":false});
            var Q14;
            Q14=makeQuery(id+"F2.opExtrude","CAP_EDGE",EDGE,{"disambiguationData":[OSD([sQuery(id+"F1.wireOp",EDGE,"E4.8.0")])],"isStart":false});
            var Q15;
            Q15=makeQuery(id+"F3.opExtrude","CAP_EDGE",EDGE,{"disambiguationData":[OSD([sQuery(id+"F1.wireOp",EDGE,"E9.7.1")])],"isStart":false});
            var Q16;
            Q16=makeQuery(id+"F2.opExtrude","CAP_EDGE",EDGE,{"disambiguationData":[OSD([sQuery(id+"F1.wireOp",EDGE,"E4.7.0")])],"isStart":false});
            var Q17;
            Q17=makeQuery(id+"F2.opExtrude","CAP_EDGE",EDGE,{"disambiguationData":[OSD([sQuery(id+"F1.wireOp",EDGE,"E4.6.0")])],"isStart":false});
            var Q18;
            Q18=makeQuery(id+"F3.opExtrude","CAP_EDGE",EDGE,{"disambiguationData":[OSD([sQuery(id+"F1.wireOp",EDGE,"E9.6.1")])],"isStart":false});
            var Q19;
            Q19=makeQuery(id+"F4.opExtrude","CAP_EDGE",EDGE,{"disambiguationData":[OSD([sQuery(id+"F1.wireOp",EDGE,"E14.7.2")])],"isStart":false});
            var Q20;
            Q20=makeQuery(id+"F4.opExtrude","CAP_EDGE",EDGE,{"disambiguationData":[OSD([sQuery(id+"F1.wireOp",EDGE,"E14.6.2")])],"isStart":false});
            var Q21;
            Q21=makeQuery(id+"F3.opExtrude","CAP_EDGE",EDGE,{"disambiguationData":[OSD([sQuery(id+"F1.wireOp",EDGE,"E9.5.1")])],"isStart":false});
            var Q22;
            Q22=makeQuery(id+"F2.opExtrude","CAP_EDGE",EDGE,{"disambiguationData":[OSD([sQuery(id+"F1.wireOp",EDGE,"E4.5.0")])],"isStart":false});
            var Q23;
            Q23=makeQuery(id+"F4.opExtrude","CAP_EDGE",EDGE,{"disambiguationData":[OSD([sQuery(id+"F1.wireOp",EDGE,"E14.5.2")])],"isStart":false});
            var Q24;
            Q24=makeQuery(id+"F3.opExtrude","CAP_EDGE",EDGE,{"disambiguationData":[OSD([sQuery(id+"F1.wireOp",EDGE,"E9.4.1")])],"isStart":false});
            var Q25;
            Q25=makeQuery(id+"F2.opExtrude","CAP_EDGE",EDGE,{"disambiguationData":[OSD([sQuery(id+"F1.wireOp",EDGE,"E4.4.0")])],"isStart":false});
            var Q26;
            Q26=makeQuery(id+"F4.opExtrude","CAP_EDGE",EDGE,{"disambiguationData":[OSD([sQuery(id+"F1.wireOp",EDGE,"E14.4.2")])],"isStart":false});
            var Q27;
            Q27=makeQuery(id+"F4.opExtrude","CAP_EDGE",EDGE,{"disambiguationData":[OSD([sQuery(id+"F1.wireOp",EDGE,"E14.3.2")])],"isStart":false});
            var Q28;
            Q28=makeQuery(id+"F3.opExtrude","CAP_EDGE",EDGE,{"disambiguationData":[OSD([sQuery(id+"F1.wireOp",EDGE,"E9.3.1")])],"isStart":false});
            var Q29;
            Q29=makeQuery(id+"F4.opExtrude","CAP_EDGE",EDGE,{"disambiguationData":[OSD([sQuery(id+"F1.wireOp",EDGE,"E14.2.2")])],"isStart":false});
            var Q30;
            Q30=makeQuery(id+"F5.opExtrude","CAP_EDGE",EDGE,{"disambiguationData":[OSD([sQuery(id+"F1.wireOp",EDGE,"E19.2.0")])],"isStart":false});
            var Q31;
            Q31=makeQuery(id+"F5.opExtrude","CAP_EDGE",EDGE,{"disambiguationData":[OSD([sQuery(id+"F1.wireOp",EDGE,"E19.3.0")])],"isStart":false});
            var Q32;
            Q32=makeQuery(id+"F5.opExtrude","CAP_EDGE",EDGE,{"disambiguationData":[OSD([sQuery(id+"F1.wireOp",EDGE,"E19.4.0")])],"isStart":false});
            var Q33;
            Q33=makeQuery(id+"F5.opExtrude","CAP_EDGE",EDGE,{"disambiguationData":[OSD([sQuery(id+"F1.wireOp",EDGE,"E19.5.0")])],"isStart":false});
            var Q34;
            Q34=makeQuery(id+"F5.opExtrude","CAP_EDGE",EDGE,{"disambiguationData":[OSD([sQuery(id+"F1.wireOp",EDGE,"E19.6.0")])],"isStart":false});
            var Q35;
            Q35=makeQuery(id+"F5.opExtrude","CAP_EDGE",EDGE,{"disambiguationData":[OSD([sQuery(id+"F1.wireOp",EDGE,"E19.7.0")])],"isStart":false});
            var Q36;
            Q36=makeQuery(id+"F5.opExtrude","CAP_EDGE",EDGE,{"disambiguationData":[OSD([sQuery(id+"F1.wireOp",EDGE,"E19.8.0")])],"isStart":false});
            var Q37;
            Q37=makeQuery(id+"F5.opExtrude","CAP_EDGE",EDGE,{"disambiguationData":[OSD([sQuery(id+"F1.wireOp",EDGE,"E19.9.0")])],"isStart":false});
            var Q38;
            Q38=makeQuery(id+"F5.opExtrude","CAP_EDGE",EDGE,{"disambiguationData":[OSD([sQuery(id+"F1.wireOp",EDGE,"E16.0")])],"isStart":false});
            var Q39;
            Q39=makeQuery(id+"F5.opExtrude","CAP_EDGE",EDGE,{"disambiguationData":[OSD([sQuery(id+"F1.wireOp",EDGE,"E19.1.0")])],"isStart":false});
            var Q40;
            Q40=makeQuery(id+"F6.opExtrude","CAP_EDGE",EDGE,{"disambiguationData":[OSD([sQuery(id+"F1.wireOp",EDGE,"E26.7.1")])],"isStart":false});
            var Q41;
            Q41=makeQuery(id+"F6.opExtrude","CAP_EDGE",EDGE,{"disambiguationData":[OSD([sQuery(id+"F1.wireOp",EDGE,"E26.6.1")])],"isStart":false});
            var Q42;
            Q42=makeQuery(id+"F6.opExtrude","CAP_EDGE",EDGE,{"disambiguationData":[OSD([sQuery(id+"F1.wireOp",EDGE,"E26.5.1")])],"isStart":false});
            var Q43;
            Q43=makeQuery(id+"F6.opExtrude","CAP_EDGE",EDGE,{"disambiguationData":[OSD([sQuery(id+"F1.wireOp",EDGE,"E26.4.1")])],"isStart":false});
            var Q44;
            Q44=makeQuery(id+"F6.opExtrude","CAP_EDGE",EDGE,{"disambiguationData":[OSD([sQuery(id+"F1.wireOp",EDGE,"E26.3.1")])],"isStart":false});
            var Q45;
            Q45=makeQuery(id+"F6.opExtrude","CAP_EDGE",EDGE,{"disambiguationData":[OSD([sQuery(id+"F1.wireOp",EDGE,"E26.2.1")])],"isStart":false});
            var Q46;
            Q46=makeQuery(id+"F6.opExtrude","CAP_EDGE",EDGE,{"disambiguationData":[OSD([sQuery(id+"F1.wireOp",EDGE,"E26.1.1")])],"isStart":false});
            var Q47;
            Q47=makeQuery(id+"F6.opExtrude","CAP_EDGE",EDGE,{"disambiguationData":[OSD([sQuery(id+"F1.wireOp",EDGE,"E21.0")])],"isStart":false});
            chamfer(context, id + "F7", {"entities" : qUnion([Q0, Q1, Q2, Q3, Q4, Q5, Q6, Q7, Q8, Q9, Q10, Q11, Q12, Q13, Q14, Q15, Q16, Q17, Q18, Q19, Q20, Q21, Q22, Q23, Q24, Q25, Q26, Q27, Q28, Q29, Q30, Q31, Q32, Q33, Q34, Q35, Q36, Q37, Q38, Q39, Q40, Q41, Q42, Q43, Q44, Q45, Q46, Q47]), "width" : 5 * mm, "tangentPropagation" : true});
        }
    });
